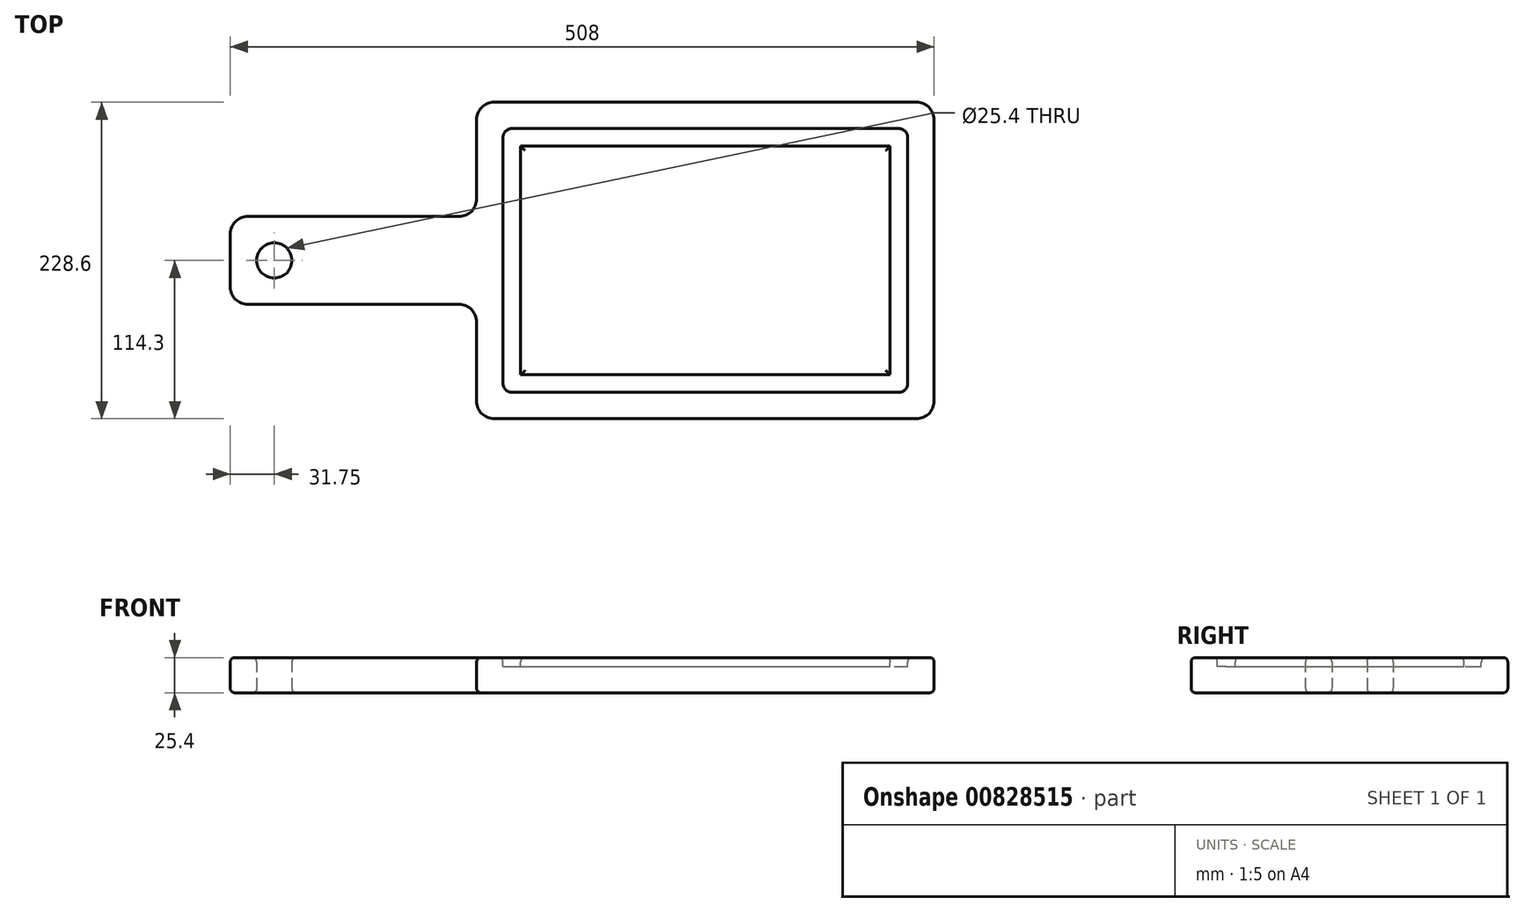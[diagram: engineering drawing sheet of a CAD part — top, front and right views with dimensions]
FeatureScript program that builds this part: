
annotation { "Feature Type Name" : "Feature", "Feature Type Description" : "" }
export const myFeature = defineFeature(function(context is Context, id is Id, definition is map)
    precondition{}
    {
        {
            var Q0;
            Q0=qCreatedBy(makeId("Top.planeOp"),FACE);
            var sketch = newSketch(context, id + "F0", { "sketchPlane" : qUnion([Q0])});
            skLineSegment(sketch, "E0.bottom", {"start": v(0, 0) * mm, "end": v(330.2, 0) * mm});
            skLineSegment(sketch, "E0.top", {"start": v(0, 228.6) * mm, "end": v(330.2, 228.6) * mm});
            skLineSegment(sketch, "E0.left", {"start": v(0, 0) * mm, "end": v(0, 228.6) * mm});
            skLineSegment(sketch, "E0.right", {"start": v(330.2, 0) * mm, "end": v(330.2, 228.6) * mm});
            skLineSegment(sketch, "E1.bottom", {"start": v(0, 146.05) * mm, "end": v(-177.8, 146.05) * mm});
            skLineSegment(sketch, "E1.top", {"start": v(0, 82.55) * mm, "end": v(-177.8, 82.55) * mm});
            skLineSegment(sketch, "E1.left", {"start": v(0, 146.05) * mm, "end": v(0, 82.55) * mm});
            skLineSegment(sketch, "E1.right", {"start": v(-177.8, 146.05) * mm, "end": v(-177.8, 82.55) * mm});
            skSolve(sketch);
        }
        {
            var Q0;
            {var subQ3=sQuery(id+"F0.wireOp",EDGE,"E0.bottom");Q0=makeQuery(id+"F0.imprint","IMPRINT",FACE,{"disambiguationData":[TD([[makeQuery(id+"F0.imprint","IMPRINT",EDGE,{"derivedFrom":subQ3}),1.0]])]});}
            var Q1;
            Q1=makeQuery(id+"F0.imprint","IMPRINT",FACE,{"disambiguationData":[TD([[makeQuery(id+"F0.imprint","IMPRINT",EDGE,{"derivedFrom":sQuery(id+"F0.wireOp",EDGE,"E1.bottom")}),1.0]])]});
            extrude(context, id + "F1", {"entities" : qUnion([Q0, Q1]), "depth" : 25.4 * mm, "offsetDistance" : 25.4 * mm});
        }
        {
            var Q0;
            Q0=makeQuery(id+"F1.opExtrude","CAP_FACE",FACE,{"disambiguationData":[OSD([sQuery(id+"F0.wireOp",EDGE,"E0.bottom"),sQuery(id+"F0.wireOp",EDGE,"E0.top"),sQuery(id+"F0.wireOp",EDGE,"E0.left"),sQuery(id+"F0.wireOp",EDGE,"E0.right"),sQuery(id+"F0.wireOp",EDGE,"E1.bottom"),sQuery(id+"F0.wireOp",EDGE,"E1.top"),sQuery(id+"F0.wireOp",EDGE,"E1.right")])],"isStart":true});
            var sketch = newSketch(context, id + "F2", { "sketchPlane" : qUnion([Q0])});
            skCircle(sketch, "E2", {"center": v(-146.05, -114.3) * mm, "radius": 12.7 * mm});
            skSolve(sketch);
        }
        {
            var Q0;
            Q0=makeQuery(id+"F2.imprint","IMPRINT",FACE,{"disambiguationData":[TD([[makeQuery(id+"F2.imprint","IMPRINT",EDGE,{"derivedFrom":sQuery(id+"F2.wireOp",EDGE,"E2")}),1.0]])]});
            var Q1;
            Q1=sQuery(id+"F2.wireOp",EDGE,"E2");
            extrude(context, id + "F3", {"entities" : qUnion([Q0]), "operationType" : NewBodyOperationType.REMOVE, "surfaceEntities" : qUnion([Q1]), "oppositeDirection" : true, "depth" : 25.4 * mm, "offsetDistance" : 25.4 * mm});
        }
        {
            var Q0;
            Q0=makeQuery(id+"F1.opExtrude","CAP_FACE",FACE,{"disambiguationData":[OSD([sQuery(id+"F0.wireOp",EDGE,"E0.bottom"),sQuery(id+"F0.wireOp",EDGE,"E0.top"),sQuery(id+"F0.wireOp",EDGE,"E0.left"),sQuery(id+"F0.wireOp",EDGE,"E0.right"),sQuery(id+"F0.wireOp",EDGE,"E1.bottom"),sQuery(id+"F0.wireOp",EDGE,"E1.top"),sQuery(id+"F0.wireOp",EDGE,"E1.right")])],"isStart":false});
            var sketch = newSketch(context, id + "F4", { "sketchPlane" : qUnion([Q0])});
            skLineSegment(sketch, "E3.0", {"start": v(19.05, 19.05) * mm, "end": v(19.05, 82.55) * mm});
            skLineSegment(sketch, "E3.1", {"start": v(19.05, 146.05) * mm, "end": v(19.05, 209.55) * mm});
            skLineSegment(sketch, "E3.2", {"start": v(19.05, 209.55) * mm, "end": v(311.15, 209.55) * mm});
            skLineSegment(sketch, "E3.3", {"start": v(311.15, 19.05) * mm, "end": v(311.15, 209.55) * mm});
            skLineSegment(sketch, "E3.4", {"start": v(19.05, 19.05) * mm, "end": v(311.15, 19.05) * mm});
            skLineSegment(sketch, "E4", {"start": v(19.05, 146.05) * mm, "end": v(19.05, 82.55) * mm});
            skLineSegment(sketch, "E5.0", {"start": v(31.75, 146.05) * mm, "end": v(31.75, 196.85) * mm});
            skLineSegment(sketch, "E5.1", {"start": v(298.45, 31.75) * mm, "end": v(298.45, 196.85) * mm});
            skLineSegment(sketch, "E5.2", {"start": v(31.75, 31.75) * mm, "end": v(298.45, 31.75) * mm});
            skLineSegment(sketch, "E5.3", {"start": v(31.75, 196.85) * mm, "end": v(298.45, 196.85) * mm});
            skLineSegment(sketch, "E5.4", {"start": v(31.75, 31.75) * mm, "end": v(31.75, 82.55) * mm});
            skLineSegment(sketch, "E5.5", {"start": v(31.75, 146.05) * mm, "end": v(31.75, 82.55) * mm});
            skSolve(sketch);
        }
        {
            var Q0;
            Q0=makeQuery(id+"F4.imprint","IMPRINT",FACE,{"disambiguationData":[TD([[makeQuery(id+"F4.imprint","IMPRINT",EDGE,{"derivedFrom":sQuery(id+"F4.wireOp",EDGE,"E3.0")}),-1.0]])]});
            extrude(context, id + "F5", {"entities" : qUnion([Q0]), "operationType" : NewBodyOperationType.REMOVE, "oppositeDirection" : true, "depth" : 6.35 * mm, "offsetDistance" : 25.4 * mm});
        }
        {
            var Q0;
            Q0=makeQuery(id+"F5.boolean.opBoolean","COPY",EDGE,{"derivedFrom":makeQuery(id+"F5.opExtrude","SWEPT_EDGE",EDGE,{"disambiguationData":[OSD([sQuery(id+"F4.wireOp",EDGE,"E3.1"),sQuery(id+"F4.wireOp",EDGE,"E3.2")])]})});
            var Q1;
            Q1=makeQuery(id+"F5.boolean.opBoolean","COPY",EDGE,{"derivedFrom":makeQuery(id+"F5.opExtrude","SWEPT_EDGE",EDGE,{"disambiguationData":[OSD([sQuery(id+"F4.wireOp",EDGE,"E3.2"),sQuery(id+"F4.wireOp",EDGE,"E3.3")])]})});
            var Q2;
            Q2=makeQuery(id+"F5.boolean.opBoolean","COPY",EDGE,{"derivedFrom":makeQuery(id+"F5.opExtrude","SWEPT_EDGE",EDGE,{"disambiguationData":[OSD([sQuery(id+"F4.wireOp",EDGE,"E3.3"),sQuery(id+"F4.wireOp",EDGE,"E3.4")])]})});
            var Q3;
            Q3=makeQuery(id+"F5.boolean.opBoolean","COPY",EDGE,{"derivedFrom":makeQuery(id+"F5.opExtrude","SWEPT_EDGE",EDGE,{"disambiguationData":[OSD([sQuery(id+"F4.wireOp",EDGE,"E3.0"),sQuery(id+"F4.wireOp",EDGE,"E3.4")])]})});
            fillet(context, id + "F6", {"entities" : qUnion([Q0, Q1, Q2, Q3]), "radius" : 6.35 * mm, "tangentPropagation" : true, "allowEdgeOverflow" : false});
        }
        {
            var Q0;
            Q0=makeQuery(id+"F1.opExtrude","SWEPT_EDGE",EDGE,{"disambiguationData":[OSD([sQuery(id+"F0.wireOp",EDGE,"E0.bottom"),sQuery(id+"F0.wireOp",EDGE,"E0.left")])]});
            var Q1;
            Q1=makeQuery(id+"F1.opExtrude","SWEPT_EDGE",EDGE,{"disambiguationData":[OSD([sQuery(id+"F0.wireOp",EDGE,"E0.bottom"),sQuery(id+"F0.wireOp",EDGE,"E0.right")])]});
            var Q2;
            Q2=makeQuery(id+"F1.opExtrude","SWEPT_EDGE",EDGE,{"disambiguationData":[OSD([sQuery(id+"F0.wireOp",EDGE,"E0.top"),sQuery(id+"F0.wireOp",EDGE,"E0.right")])]});
            var Q3;
            Q3=makeQuery(id+"F1.opExtrude","SWEPT_EDGE",EDGE,{"disambiguationData":[OSD([sQuery(id+"F0.wireOp",EDGE,"E0.top"),sQuery(id+"F0.wireOp",EDGE,"E0.left")])]});
            var Q4;
            Q4=makeQuery(id+"F1.opExtrude","SWEPT_EDGE",EDGE,{"disambiguationData":[OSD([sQuery(id+"F0.wireOp",EDGE,"E1.top"),sQuery(id+"F0.wireOp",EDGE,"E1.right")])]});
            var Q5;
            Q5=makeQuery(id+"F1.opExtrude","SWEPT_EDGE",EDGE,{"disambiguationData":[OSD([sQuery(id+"F0.wireOp",EDGE,"E1.bottom"),sQuery(id+"F0.wireOp",EDGE,"E1.right")])]});
            var Q6;
            Q6=makeQuery(id+"F1.opExtrude","SWEPT_EDGE",EDGE,{"disambiguationData":[OSD([sQuery(id+"F0.wireOp",EDGE,"E0.left"),sQuery(id+"F0.wireOp",EDGE,"E1.bottom"),sQuery(id+"F0.wireOp",EDGE,"E1.left")])]});
            var Q7;
            Q7=makeQuery(id+"F1.opExtrude","SWEPT_EDGE",EDGE,{"disambiguationData":[OSD([sQuery(id+"F0.wireOp",EDGE,"E0.left"),sQuery(id+"F0.wireOp",EDGE,"E1.top"),sQuery(id+"F0.wireOp",EDGE,"E1.left")])]});
            fillet(context, id + "F7", {"entities" : qUnion([Q0, Q1, Q2, Q3, Q4, Q5, Q6, Q7]), "radius" : 12.7 * mm, "tangentPropagation" : true, "allowEdgeOverflow" : false});
        }
        {
            var Q0;
            Q0=makeQuery(id+"F5.boolean.opBoolean","SPLIT",FACE,{"disambiguationData":[TD([makeQuery(id+"F5.opExtrude","SWEPT_FACE",FACE,{"disambiguationData":[OSD([sQuery(id+"F4.wireOp",EDGE,"E5.1")])]})])],"derivedFrom":makeQuery(id+"F1.opExtrude","CAP_FACE",FACE,{"disambiguationData":[OSD([sQuery(id+"F0.wireOp",EDGE,"E0.bottom"),sQuery(id+"F0.wireOp",EDGE,"E0.top"),sQuery(id+"F0.wireOp",EDGE,"E0.left"),sQuery(id+"F0.wireOp",EDGE,"E0.right"),sQuery(id+"F0.wireOp",EDGE,"E1.bottom"),sQuery(id+"F0.wireOp",EDGE,"E1.top"),sQuery(id+"F0.wireOp",EDGE,"E1.right")])],"isStart":false})});
            var Q1;
            {var subQ0=sQuery(id+"F0.wireOp",EDGE,"E1.right");var subQ1=sQuery(id+"F0.wireOp",EDGE,"E1.top");var subQ2=sQuery(id+"F0.wireOp",EDGE,"E1.bottom");var subQ3=sQuery(id+"F0.wireOp",EDGE,"E0.right");var subQ4=sQuery(id+"F0.wireOp",EDGE,"E0.bottom");var subQ5=sQuery(id+"F0.wireOp",EDGE,"E0.left");var subQ6=sQuery(id+"F0.wireOp",EDGE,"E0.top");Q1=makeQuery(id+"F5.boolean.opBoolean","SPLIT",FACE,{"disambiguationData":[TD([makeQuery(id+"F1.opExtrude","SWEPT_FACE",FACE,{"disambiguationData":[OSD([subQ4])]})])],"derivedFrom":makeQuery(id+"F1.opExtrude","CAP_FACE",FACE,{"disambiguationData":[OSD([subQ4,subQ6,subQ5,subQ3,subQ2,subQ1,subQ0])],"isStart":false})});}
            var Q2;
            Q2=makeQuery(id+"F1.opExtrude","CAP_FACE",FACE,{"disambiguationData":[OSD([sQuery(id+"F0.wireOp",EDGE,"E0.bottom"),sQuery(id+"F0.wireOp",EDGE,"E0.top"),sQuery(id+"F0.wireOp",EDGE,"E0.left"),sQuery(id+"F0.wireOp",EDGE,"E0.right"),sQuery(id+"F0.wireOp",EDGE,"E1.bottom"),sQuery(id+"F0.wireOp",EDGE,"E1.top"),sQuery(id+"F0.wireOp",EDGE,"E1.right")])],"isStart":true});
            fillet(context, id + "F8", {"entities" : qUnion([Q0, Q1, Q2]), "radius" : 3.17 * mm, "tangentPropagation" : true, "allowEdgeOverflow" : false});
        }
    });
